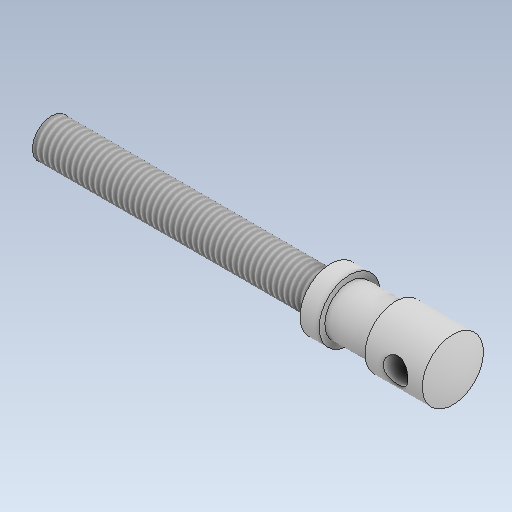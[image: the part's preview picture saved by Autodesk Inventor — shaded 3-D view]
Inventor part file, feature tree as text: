
AUTODESK INVENTOR PART (.ipt)
format: ipt  version: 2021 (Build 250183000, 183)  size: 156,672 bytes
history: native  units: mm
features: other x3, sketch x2, thread x1, extrude x1
ambient origin geometry x8: Origin, YZ Plane, XZ Plane, XY Plane, X Axis, Y Axis, Z Axis, Center Point
bodies: Body1 (feature_tree)
feature tree (7):
  other  "Sólido1"
  other  "Revolução1"
  thread  "Rosca1"  [1 undecoded]
  extrude  "Extrusão1"  Depth=5.0mm
  sketch  "Esboço1"  dims[d2=73.0mm d4=5.0mm]
  sketch  "Esboço2"  dims[d6=12.0mm d8=15.0mm d9=10.0mm d10=16.0mm d11=13.0mm d12=16.0mm d13=90.0deg d14=73.0mm d15=0.0mm d16=6.5mm d17=7.0mm d18=0.0mm d19=0.0mm]
  other  "Projetar arestas de corte1"
note: 1 required parameter value undecoded (feature->parameter linkage not recoverable at this tier; creation-order binding heuristic only, values carry confidence <= 0.55)
